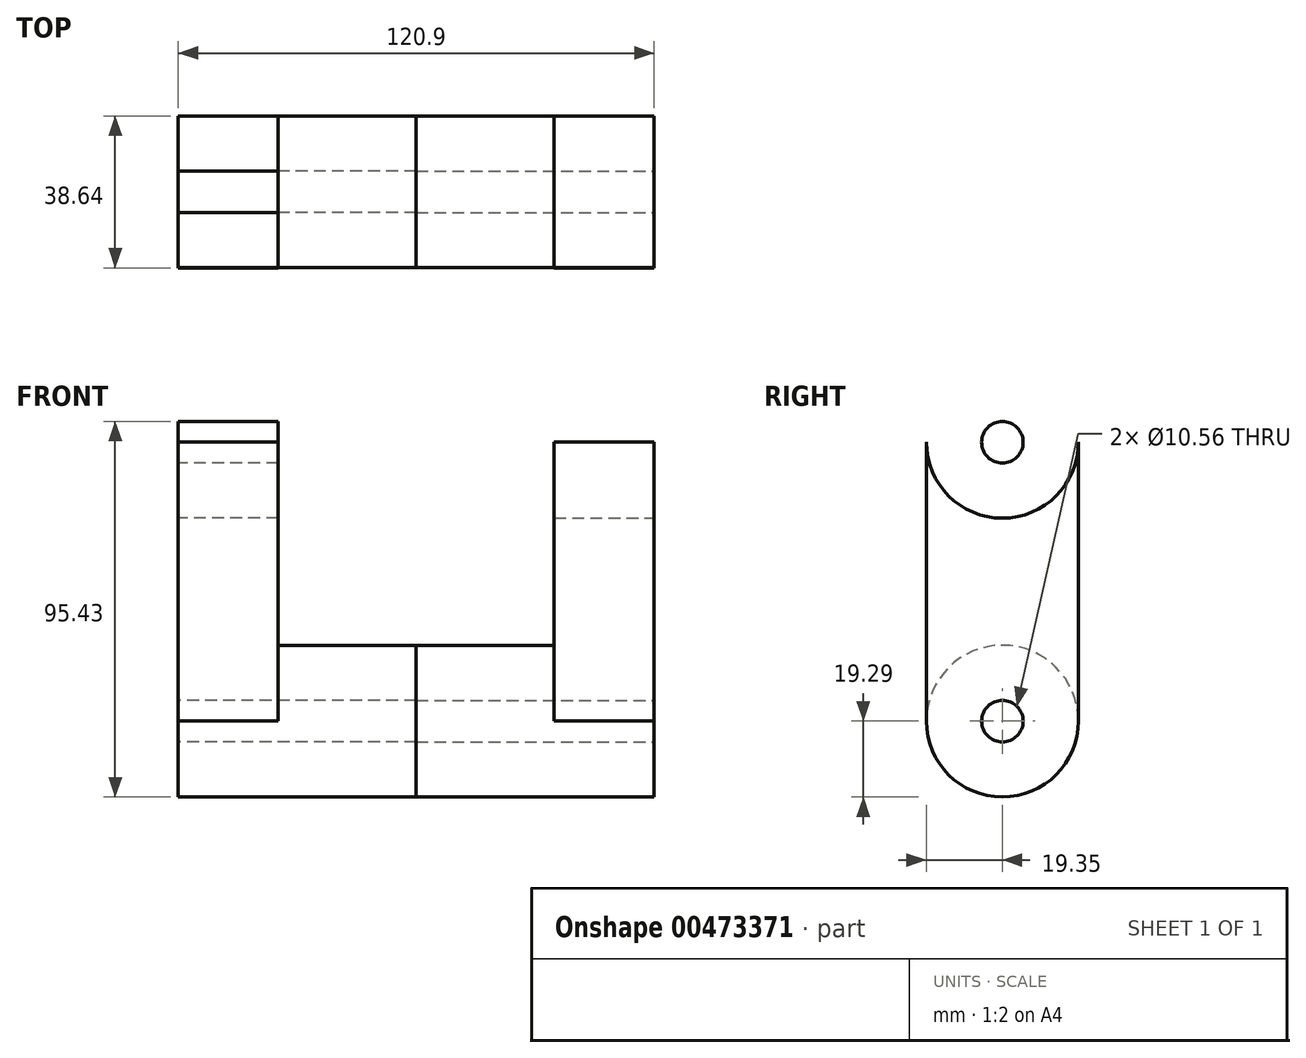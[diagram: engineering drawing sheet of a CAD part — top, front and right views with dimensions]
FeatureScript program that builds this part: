
annotation { "Feature Type Name" : "Feature", "Feature Type Description" : "" }
export const myFeature = defineFeature(function(context is Context, id is Id, definition is map)
    precondition{}
    {
        {
            var Q0;
            Q0=qCreatedBy(makeId("Right.planeOp"),FACE);
            var sketch = newSketch(context, id + "F0", { "sketchPlane" : qUnion([Q0])});
            skCircle(sketch, "E0", {"center": v(0, 0) * mm, "radius": 19.3 * mm});
            skLineSegment(sketch, "E1.left", {"start": v(19.3, 0) * mm, "end": v(19.3, 70.86) * mm});
            skLineSegment(sketch, "E1.right", {"start": v(-19.35, 0) * mm, "end": v(-19.35, 70.86) * mm});
            skCircle(sketch, "E2.MirrorC", {"center": v(0, 70.86) * mm, "radius": 19.3 * mm});
            skLineSegment(sketch, "E3.trimOffspring", {"start": v(-19.3, 0) * mm, "end": v(-19.35, 0) * mm});
            skLineSegment(sketch, "E4.trimOffspring", {"start": v(-19.3, 70.86) * mm, "end": v(-19.35, 70.86) * mm});
            skPoint(sketch, "E5.end.orphan", {"position": v(-19.35, 35.43) * mm});
            skPoint(sketch, "E5.start.orphan", {"position": v(19.3, 35.43) * mm});
            skCircle(sketch, "E6", {"center": v(0, 0) * mm, "radius": 5.28 * mm});
            skCircle(sketch, "E7.MirrorC", {"center": v(0, 70.86) * mm, "radius": 5.28 * mm});
            skSolve(sketch);
        }
        {
            var Q0;
            {var subQ0=sQuery(id+"F0.wireOp",EDGE,"E3.trimOffspring");Q0=makeQuery(id+"F0.imprint","IMPRINT",FACE,{"disambiguationData":[TD([[makeQuery(id+"F0.imprint","IMPRINT",EDGE,{"derivedFrom":subQ0}),-1.0]])]});}
            var Q1;
            {var subQ0=sQuery(id+"F0.wireOp",EDGE,"E4.trimOffspring");Q1=makeQuery(id+"F0.imprint","IMPRINT",FACE,{"disambiguationData":[TD([[makeQuery(id+"F0.imprint","IMPRINT",EDGE,{"derivedFrom":subQ0}),1.0]])]});}
            var Q2;
            Q2=makeQuery(id+"F0.imprint","IMPRINT",FACE,{"disambiguationData":[TD([[makeQuery(id+"F0.imprint","IMPRINT",EDGE,{"derivedFrom":sQuery(id+"F0.wireOp",EDGE,"E7.MirrorC")}),1.0]])]});
            extrude(context, id + "F1", {"entities" : qUnion([Q0, Q1, Q2]), "depth" : 25.4 * mm});
        }
        {
            var Q0;
            Q0=makeQuery(id+"F0.imprint","IMPRINT",FACE,{"disambiguationData":[TD([[makeQuery(id+"F0.imprint","IMPRINT",EDGE,{"derivedFrom":sQuery(id+"F0.wireOp",EDGE,"E6")}),-1.0]])]});
            extrude(context, id + "F2", {"entities" : qUnion([Q0]), "operationType" : NewBodyOperationType.ADD, "depth" : 60.45 * mm});
        }
        {
            var Q0;
            Q0=makeQuery(id+"F1.opExtrude","SWEPT_BODY",BODY,{"disambiguationData":[OSD([sQuery(id+"F0.wireOp",EDGE,"E0"),sQuery(id+"F0.wireOp",EDGE,"E1.left"),sQuery(id+"F0.wireOp",EDGE,"E1.right"),sQuery(id+"F0.wireOp",EDGE,"E2.MirrorC"),sQuery(id+"F0.wireOp",EDGE,"E3.trimOffspring"),sQuery(id+"F0.wireOp",EDGE,"E4.trimOffspring"),sQuery(id+"F0.wireOp",EDGE,"E7.MirrorC")])]});
            var Q1;
            Q1=makeQuery(id+"F2.opExtrude","CAP_FACE",FACE,{"disambiguationData":[OSD([sQuery(id+"F0.wireOp",EDGE,"E0"),sQuery(id+"F0.wireOp",EDGE,"E6")])],"isStart":false});
            mirror(context, id + "F3", {"entities" : qUnion([Q0]), "mirrorPlane" : qUnion([Q1])});
        }
    });
